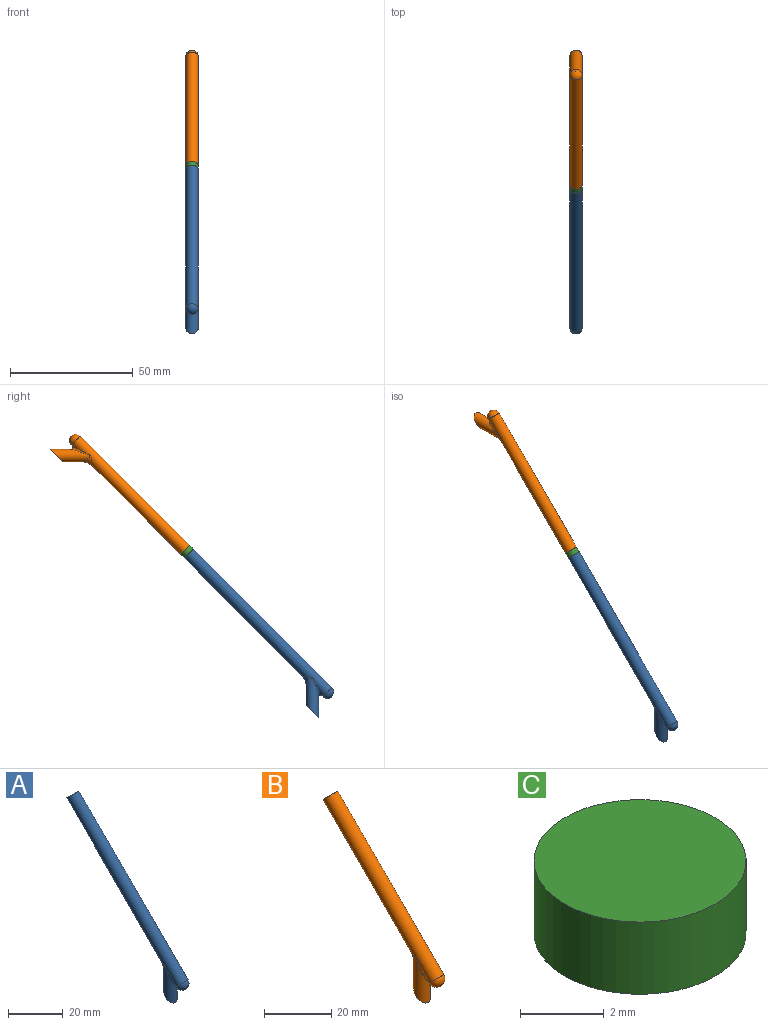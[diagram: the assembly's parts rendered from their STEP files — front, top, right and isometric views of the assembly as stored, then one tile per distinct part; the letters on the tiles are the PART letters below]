
ASSEMBLY  parts=3 mates=2
PART A: 7 faces, bbox 6.1x61.9x69.8 mm
  f0: cylinder r=2.54mm len=60.11mm, axis (0,-0.71,-0.71), area 1217.6mm2, adj f1,f2,f5,f6
  f1: plane 5.08x3.59mm, normal (0,0.71,0.71), area 20.3mm2, adj f0
  f2: sphere r=2.54mm, area 40.5mm2, adj f0
  f3: cylinder r=2.54mm len=16.51mm, axis (0,0,-1), area 163.5mm2, adj f4,f5,f6
  f4: plane 6.15x6.15mm, normal (0,0.71,-0.71), area 28.7mm2, adj f3
  f5: bspline ~8.28x5.08mm, area 17.1mm2, adj f0,f3
  f6: bspline ~5.08x4.03mm, area 21.2mm2, adj f0,f3
PART B: 7 faces, bbox 6.1x50x57.8 mm
  f0: cylinder r=2.54mm len=48.18mm, axis (0,-0.71,-0.71), area 948.3mm2, adj f1,f2,f5,f6
  f1: plane 5.08x3.59mm, normal (0,0.71,0.71), area 20.3mm2, adj f0
  f2: sphere r=2.54mm, area 40.5mm2, adj f0
  f3: cylinder r=2.54mm len=16.51mm, axis (0,0,-1), area 163.5mm2, adj f4,f5,f6
  f4: plane 6.15x6.15mm, normal (0,0.71,-0.71), area 28.7mm2, adj f3
  f5: bspline ~8.28x5.08mm, area 17.1mm2, adj f0,f3
  f6: bspline ~5.08x4.03mm, area 20.9mm2, adj f0,f3
PART C: 3 faces, bbox 5.1x5.1x2.1 mm
  f0: cylinder r=2.54mm len=5.08mm, axis (0,0,-1), area 33.8mm2, adj f1,f2
  f1: plane 5.08x5.08mm, normal (0,0,1), area 20.3mm2, adj f0
  f2: plane 5.08x5.08mm, normal (0,0,-1), area 20.3mm2, adj f0
PLACE A t=(28.98,-27.7,61.41)mm
PLACE B rot(axis=(0,0.71,-0.71),180deg) t=(28.98,79.15,168.27)mm
PLACE C rot(axis=(0,0.38,0.92),180deg) t=(28.98,22.68,128.31)mm
MATE fastened C.f0 <-> B.f0  axis (0,0.71,0.71) through (28.98,24.18,129.81)mm
MATE fastened C.f0 <-> A.f0  axis (0,-0.71,-0.71) through (28.98,22.68,128.31)mm
